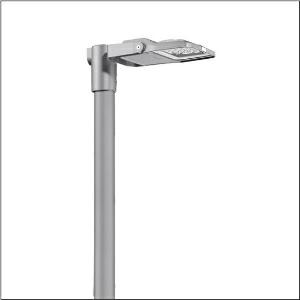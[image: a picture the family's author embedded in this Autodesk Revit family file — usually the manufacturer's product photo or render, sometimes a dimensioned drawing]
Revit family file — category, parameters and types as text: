
# Revit family: floodlight_fl_21_iq_micro___pl61_5xa7761a4c3a_000e
name_source: partatom
category: Lighting Fixtures
units: mm (PartAtom-declared; Revit-internal decimal feet)

## family parameters
Cut with Voids When Loaded = No
Host = Face
Light Source = No
Part Type = Normal
Room Calculation Point = No
Round Connector Dimension = Use Diameter
Shared = No

## types (1)
- --- (1 x LED, 3030 lm, 23.1 W, 4000K)
    Apparent Load = 23 VA
    CIE Flux Codes = 33 65 98 100 100
    Color Rendering = 70
    Color Temperature = 4000K
    Default Elevation = 1800 mm
    Description = Floodlight FL 21 iQ micro, floodlight, primary light control with lens, of PMMA, primary optical cover: protective disc, of toughened safety glass, transparent, light distribution: PL61, light emission: direct distribution, installation type: surface-mounted, LED, High Power LED, rated luminous flux: 3.030lm, luminous efficacy: 131lm/W, light colour: 740, colour temperature: 4000K, control: optimised constant luminous flux control (CLO 2.0), Desk-Remote (wireless, voltage-free reading and setting of iQ features in the workshop via application-optimized NFC function/RFID function), Light-Fading, Smart-Wire, Night-Set, Lumen-Switch, Temp-Guard, Auto-Match, with terminal, 6-pole, mains connection: 220..240V, AC, 50/60Hz, start of lifetime: 23W, end of service life: 24W, reduction: 11W, luminaire housing, of diecast aluminium, powder-coated, Siteco® metallic grey (DB 702S), corrosivity category C5 mid according to DIN EN ISO 12944, sealing non-destructively replaceable, please order mast flange separately, mast bracket, of steel, galvanised, powder-coated, Siteco® metallic grey (DB 702S), protection rating (complete): IP66, insulation class (complete): insulation class II (safety insulation), certification: CE, ENEC, VDE, protection symbol: D, impact resistance: IK07, permissible operating ambient temperature: -40..+40°C, permissible operating ambient temperature for outdoor applications: -40..+50°C, standard: DIN EN 12944, LABS conformity tested according to VDMA 24364:2018-05, packaging unit: 1 piece

Light Distribution: PL61
    Height = 65 mm
    Lamp = 1 x LED
    Lamp Light Flux = 3030 lm
    Lamp Power = 23.1 W
    Lamp count = 1
    Length = 312 mm
    Luminous efficacy = 131 lm/W
    Manufacturer = Siteco
    ModVariant = No
    Model = 5XA7761A4C3A
    Number of Poles = 1
    OnlyDefault = Yes
    Power Factor = 1
    Product Name = Floodlight FL 21 iQ micro | PL61
    Product group = floodlight | pylon annexe
    ProductGroupID = 6200
    Protection Class = Protection class II
    Protection Degree = IP 66
    RLX_Detail_Level = 1
    RLX_Emergency_Light_Flux = 0 lm
    RLX_Emergency_Type = 0
    RLX_Emergency_Type_DB = No
    RlxData = <blob elided: 101985 chars, md5=f660cc64>
    Socket = socket
    Standby Power = 0 W
    System Light Flux = 3030 lm
    System Power = 23 W
    Type Comments = factory setting: luminous flux: 100 % | dim-lin: 254 | 455 mA
    Type Image = l_1007121.jpg
    URL = http://relux.com
    VarID = @adj_129019
    Voltage = 0 V
    Weight = 0.00 kg
    Width = 230 mm

## geometry (parser evidence)
native form markers: Blend x4, Sweep x14
no freeform markers — native parametric forms only
